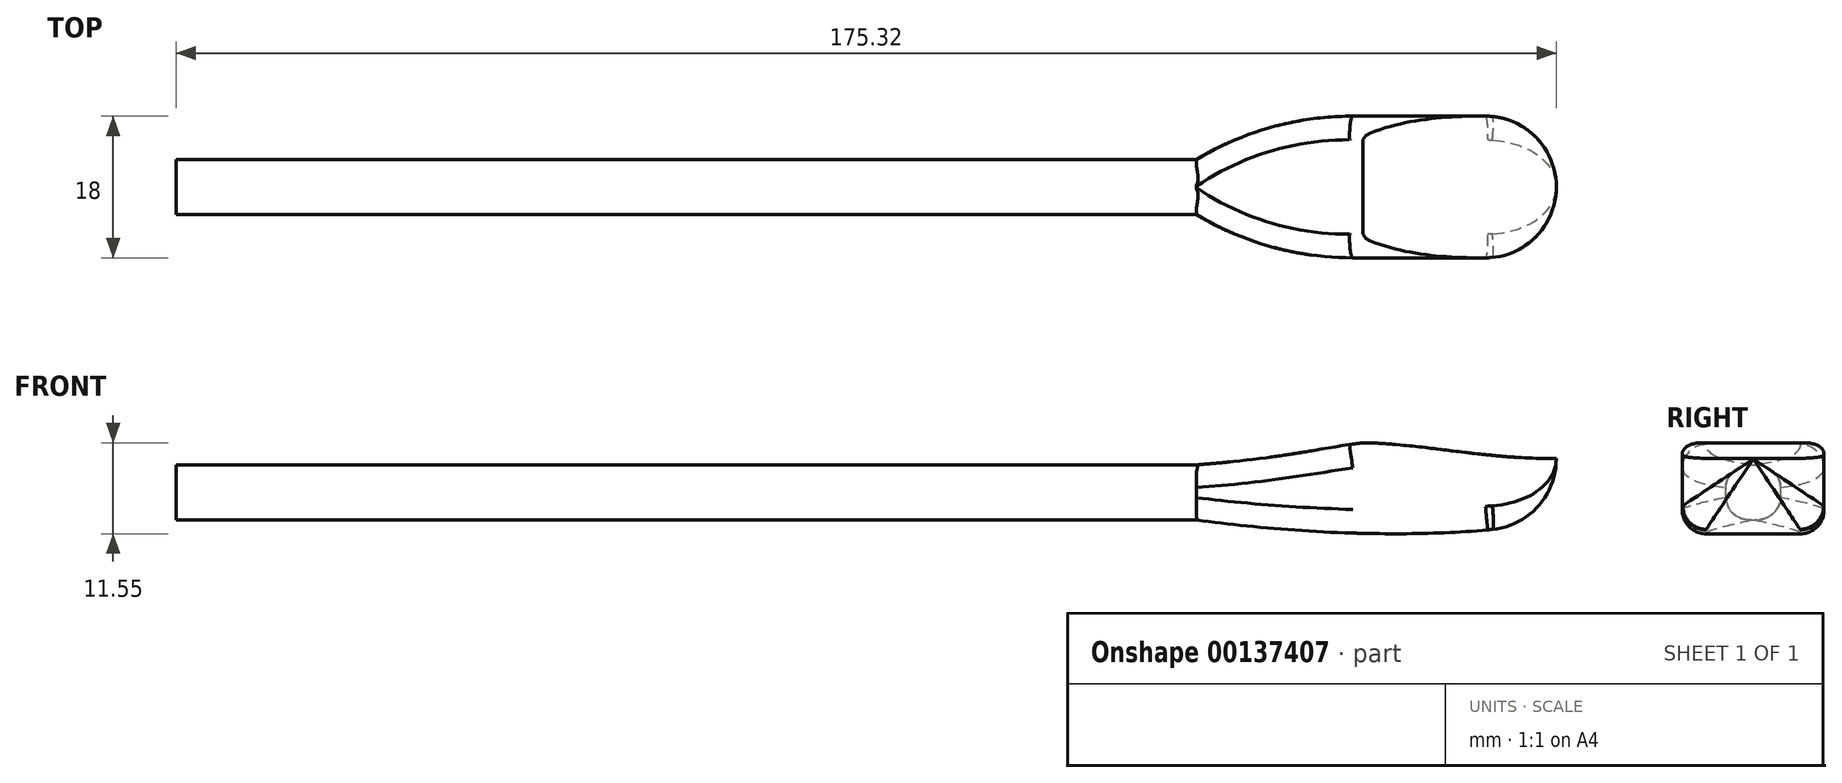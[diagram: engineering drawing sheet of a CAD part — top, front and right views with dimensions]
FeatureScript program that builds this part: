
annotation { "Feature Type Name" : "Feature", "Feature Type Description" : "" }
export const myFeature = defineFeature(function(context is Context, id is Id, definition is map)
    precondition{}
    {
        {
            var Q0;
            Q0=qCreatedBy(makeId("Front.planeOp"),FACE);
            var sketch = newSketch(context, id + "F0", { "sketchPlane" : qUnion([Q0])});
            skLineSegment(sketch, "E0", {"start": v(-68.32, 0) * mm, "end": v(-68.32, 7) * mm});
            skLineSegment(sketch, "E1", {"start": v(-68.32, 7) * mm, "end": v(66.58, 7) * mm});
            skLineSegment(sketch, "E2", {"start": v(66.58, 0) * mm, "end": v(-68.32, 0) * mm});
            skPoint(sketch, "E3", {"position": v(89.98, 7) * mm});
            skCircle(sketch, "E4", {"center": v(-72.76, 3.45) * mm, "radius": 4.25 * mm});
            skLineSegment(sketch, "E5", {"start": v(-67.27, 7) * mm, "end": v(-72.76, 7.7) * mm});
            skLineSegment(sketch, "E6", {"start": v(-67.27, 0) * mm, "end": v(-72.76, -0.8) * mm});
            skPoint(sketch, "E7.startSnap0", {"position": v(113.8, 3.85) * mm});
            skFitSpline(sketch, "E8", {"points": [v(82.44, 9.8) * mm, v(107, 7.81) * mm], "startDerivative": vector(19.24, 0.07) * mm, "endDerivative": vector(25.33, 0.47) * mm});
            skLineSegment(sketch, "E9", {"start": v(61.26, 0) * mm, "end": v(61.26, 7) * mm});
            skFitSpline(sketch, "E10", {"points": [v(61.26, 7) * mm, v(82.44, 9.8) * mm], "startDerivative": vector(33.85, 2.53) * mm, "endDerivative": vector(14.51, 1.62) * mm});
            skLineSegment(sketch, "E11", {"start": v(98.65, 8.23) * mm, "end": v(98.65, 5.73) * mm});
            skArc(sketch, "E12", {"start": v(107, 0) * mm, "mid": v(107.79, 3.9) * mm, "end": v(107, 7.81) * mm});
            skLineSegment(sketch, "E13", {"start": v(107, 7.81) * mm, "end": v(107, 0) * mm});
            skFitSpline(sketch, "E14", {"points": [v(61.26, 0) * mm, v(88.2, -1.74) * mm, v(107, 0) * mm], "startDerivative": vector(52.9, -7.14) * mm, "endDerivative": vector(38.04, 7.67) * mm});
            skLineSegment(sketch, "E15", {"start": v(82.44, 9.8) * mm, "end": v(82.44, -1.7) * mm});
            skLineSegment(sketch, "E16", {"start": v(61.26, 7) * mm, "end": v(82.44, 7) * mm});
            skLineSegment(sketch, "E17", {"start": v(82.44, 7) * mm, "end": v(82.44, 9.8) * mm});
            skSolve(sketch);
        }
        {
            var Q0;
            {var subQ1=sQuery(id+"F0.wireOp",EDGE,"E13");Q0=makeQuery(id+"F0.imprint","IMPRINT",FACE,{"disambiguationData":[TD([[makeQuery(id+"F0.imprint","IMPRINT",EDGE,{"derivedFrom":subQ1}),-1.0]])]});}
            var Q1;
            {var subQ1=sQuery(id+"F0.wireOp",EDGE,"E9");Q1=makeQuery(id+"F0.imprint","IMPRINT",FACE,{"disambiguationData":[TD([[makeQuery(id+"F0.imprint","IMPRINT",EDGE,{"derivedFrom":subQ1}),-1.0]])]});}
            var Q2;
            {var subQ0=sQuery(id+"F0.wireOp",EDGE,"E10");Q2=makeQuery(id+"F0.imprint","IMPRINT",FACE,{"disambiguationData":[TD([[makeQuery(id+"F0.imprint","IMPRINT",EDGE,{"derivedFrom":subQ0}),-1.0]])]});}
            extrude(context, id + "F1", {"entities" : qUnion([Q0, Q1, Q2]), "endBound" : BoundingType.SYMMETRIC, "depth" : 18 * mm});
        }
        {
            var Q0;
            {var subQ4=sQuery(id+"F0.wireOp",EDGE,"E0");Q0=makeQuery(id+"F0.imprint","IMPRINT",FACE,{"disambiguationData":[TD([[makeQuery(id+"F0.imprint","IMPRINT",EDGE,{"derivedFrom":subQ4}),-1.0]])]});}
            extrude(context, id + "F2", {"entities" : qUnion([Q0]), "operationType" : NewBodyOperationType.ADD, "endBound" : BoundingType.SYMMETRIC, "depth" : 7 * mm});
        }
        {
            var Q0;
            Q0=makeQuery(id+"F2.opExtrude","CAP_EDGE",EDGE,{"disambiguationData":[OSD([sQuery(id+"F0.wireOp",EDGE,"E2")])],"isStart":false});
            var Q1;
            Q1=makeQuery(id+"F2.opExtrude","CAP_EDGE",EDGE,{"disambiguationData":[OSD([sQuery(id+"F0.wireOp",EDGE,"E1")])],"isStart":false});
            var Q2;
            Q2=makeQuery(id+"F2.opExtrude","CAP_EDGE",EDGE,{"disambiguationData":[OSD([sQuery(id+"F0.wireOp",EDGE,"E2")])],"isStart":true});
            var Q3;
            Q3=makeQuery(id+"F2.opExtrude","CAP_EDGE",EDGE,{"disambiguationData":[OSD([sQuery(id+"F0.wireOp",EDGE,"E1")])],"isStart":true});
            fillet(context, id + "F3", {"entities" : qUnion([Q0, Q1, Q2, Q3]), "radius" : 3.05 * mm, "tangentPropagation" : true, "allowEdgeOverflow" : false});
        }
        {
            var Q0;
            Q0=makeQuery(id+"F1.opExtrude","CAP_EDGE",EDGE,{"disambiguationData":[OSD([sQuery(id+"F0.wireOp",EDGE,"E9")])],"isStart":false});
            var Q1;
            Q1=makeQuery(id+"FikQzlCO1YP5s6j_1.opFillet","BLEND_EDGE",EDGE,{"blendedFrom":[makeQuery(id+"F1.opExtrude","CAP_EDGE",EDGE,{"disambiguationData":[OSD([sQuery(id+"F0.wireOp",EDGE,"E14")])],"isStart":false}),makeQuery(id+"F1.opExtrude","SWEPT_FACE",FACE,{"disambiguationData":[OSD([sQuery(id+"F0.wireOp",EDGE,"E9")])]})],"blendedInto":[makeQuery(id+"F1.opExtrude","SWEPT_FACE",FACE,{"disambiguationData":[OSD([sQuery(id+"F0.wireOp",EDGE,"E9")])]})]});
            var Q2;
            Q2=makeQuery(id+"F1.opExtrude","CAP_EDGE",EDGE,{"disambiguationData":[OSD([sQuery(id+"F0.wireOp",EDGE,"E9")])],"isStart":true});
            fillet(context, id + "F4", {"entities" : qUnion([Q0, Q1, Q2]), "radius" : 38.69 * mm, "tangentPropagation" : true, "allowEdgeOverflow" : false});
        }
        {
            var Q0;
            Q0=makeQuery(id+"F4.opFillet","BLEND_EDGE",EDGE,{"blendedFrom":[makeQuery(id+"F1.opExtrude","CAP_EDGE",EDGE,{"disambiguationData":[OSD([sQuery(id+"F0.wireOp",EDGE,"E9")])],"isStart":false}),makeQuery(id+"F1.opExtrude","SWEPT_FACE",FACE,{"disambiguationData":[OSD([sQuery(id+"F0.wireOp",EDGE,"E10")])]})],"blendedInto":[makeQuery(id+"F1.opExtrude","SWEPT_FACE",FACE,{"disambiguationData":[OSD([sQuery(id+"F0.wireOp",EDGE,"E10")])]})]});
            var Q1;
            Q1=makeQuery(id+"F4.opFillet","BLEND_EDGE",EDGE,{"blendedFrom":[makeQuery(id+"F1.opExtrude","CAP_EDGE",EDGE,{"disambiguationData":[OSD([sQuery(id+"F0.wireOp",EDGE,"E9")])],"isStart":true}),makeQuery(id+"F1.opExtrude","SWEPT_FACE",FACE,{"disambiguationData":[OSD([sQuery(id+"F0.wireOp",EDGE,"E10")])]})],"blendedInto":[makeQuery(id+"F1.opExtrude","SWEPT_FACE",FACE,{"disambiguationData":[OSD([sQuery(id+"F0.wireOp",EDGE,"E10")])]})]});
            var Q2;
            Q2=makeQuery(id+"F4.opFillet","BLEND_EDGE",EDGE,{"blendedFrom":[makeQuery(id+"F1.opExtrude","CAP_EDGE",EDGE,{"disambiguationData":[OSD([sQuery(id+"F0.wireOp",EDGE,"E9")])],"isStart":false}),makeQuery(id+"F1.opExtrude","SWEPT_FACE",FACE,{"disambiguationData":[OSD([sQuery(id+"F0.wireOp",EDGE,"E14")])]})],"blendedInto":[makeQuery(id+"F1.opExtrude","SWEPT_FACE",FACE,{"disambiguationData":[OSD([sQuery(id+"F0.wireOp",EDGE,"E14")])]})]});
            var Q3;
            Q3=makeQuery(id+"F4.opFillet","BLEND_EDGE",EDGE,{"blendedFrom":[makeQuery(id+"F1.opExtrude","CAP_EDGE",EDGE,{"disambiguationData":[OSD([sQuery(id+"F0.wireOp",EDGE,"E9")])],"isStart":true}),makeQuery(id+"F1.opExtrude","SWEPT_FACE",FACE,{"disambiguationData":[OSD([sQuery(id+"F0.wireOp",EDGE,"E14")])]})],"blendedInto":[makeQuery(id+"F1.opExtrude","SWEPT_FACE",FACE,{"disambiguationData":[OSD([sQuery(id+"F0.wireOp",EDGE,"E14")])]})]});
            fillet(context, id + "F5", {"entities" : qUnion([Q0, Q1, Q2, Q3]), "radius" : 3 * mm, "tangentPropagation" : true, "allowEdgeOverflow" : false});
        }
        {
            var Q0;
            Q0=makeQuery(id+"F1.opExtrude","CAP_EDGE",EDGE,{"disambiguationData":[OSD([sQuery(id+"F0.wireOp",EDGE,"E13")])],"isStart":true});
            var Q1;
            Q1=makeQuery(id+"F1.opExtrude","CAP_EDGE",EDGE,{"disambiguationData":[OSD([sQuery(id+"F0.wireOp",EDGE,"E13")])],"isStart":false});
            fillet(context, id + "F6", {"entities" : qUnion([Q0, Q1]), "radius" : 9 * mm, "tangentPropagation" : true, "allowEdgeOverflow" : false});
        }
    });
